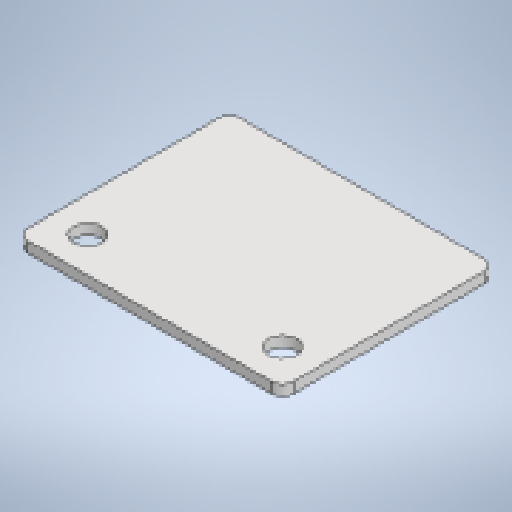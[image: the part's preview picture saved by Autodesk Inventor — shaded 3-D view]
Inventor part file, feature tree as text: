
AUTODESK INVENTOR PART (.ipt)
format: ipt  version: 2025 (Build 290162010, 162A)  size: 189,440 bytes
history: native  units: mm
features: sheet_metal_op x1, chamfer x1, sketch x1, other x1
ambient origin geometry x8: Origin, YZ Plane, XZ Plane, XY Plane, X Axis, Y Axis, Z Axis, Center Point
bodies: Body1 (feature_tree)
feature tree (4):
  sheet_metal_op  "Face3"
  chamfer  "Corner Round1"
  sketch  "Sketch1"  dims[d61=500.0mm d154=150.0mm d155=120.0mm d156=6.0mm d157=20.0mm d158=20.0mm d159=16.0mm d160=6.0mm]
  other  "Plate5"
